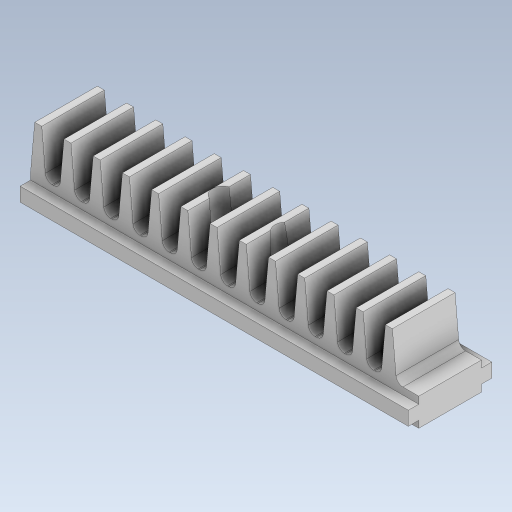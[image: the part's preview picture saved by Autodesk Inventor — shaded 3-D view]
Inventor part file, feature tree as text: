
AUTODESK INVENTOR PART (.ipt)
format: ipt  version: 2023.5 (Build 275446000, 446)  size: 573,440 bytes
history: native  units: in
note: dims shown in document units (in); Inventor stores cm internally (conversion verified against a paired STEP export)
features: extrude x4, sketch x3, fillet x2, pattern_linear x1, plane x1
ambient origin geometry x8: Origin, YZ Plane, XZ Plane, XY Plane, X Axis, Y Axis, Z Axis, Center Point
bodies: Solid1 (feature_tree)
feature tree (11):
  sketch  "Sketch1"  dims[d29=0.1378in d30=0.1181in]
  extrude  "Extrusion1"  Depth=0.1181in
  extrude  "Extrusion2"  Depth=0.0618in
  fillet  "Fillet1"  Radius=0.0309in
  pattern_linear  "Rectangular Pattern1"  Spacing1=0.0866in  [1 undecoded]
  fillet  "Fillet2"  Radius=0.1575in
  plane  "Work Plane1"
  extrude  "Extrusion3"  Depth=0.3543in TaperAngle=0.0deg
  extrude  "Extrusion4"  Depth=0.3543in TaperAngle=0.0deg
  sketch  "Sketch2"  dims[d31=0.1181in d32=0.0618in d33=0.0309in]
  sketch  "Sketch3"  dims[d34=0.0394in d35=0.0866in d36=0.1575in d37=0.3543in d38=0.0in d39=0.3543in d40=0.0in d41=0.0394in d42=5.1181in d44=0.1654in d45=0.0394in d46=0.0787in d47=0.0394in d48=0.4724in d49=0.0in d50=0.1181in d51=0.1181in d52=0.3543in d53=0.4724in d54=0.0in]
note: 1 required parameter value undecoded (feature->parameter linkage not recoverable at this tier; creation-order binding heuristic only, values carry confidence <= 0.55)
